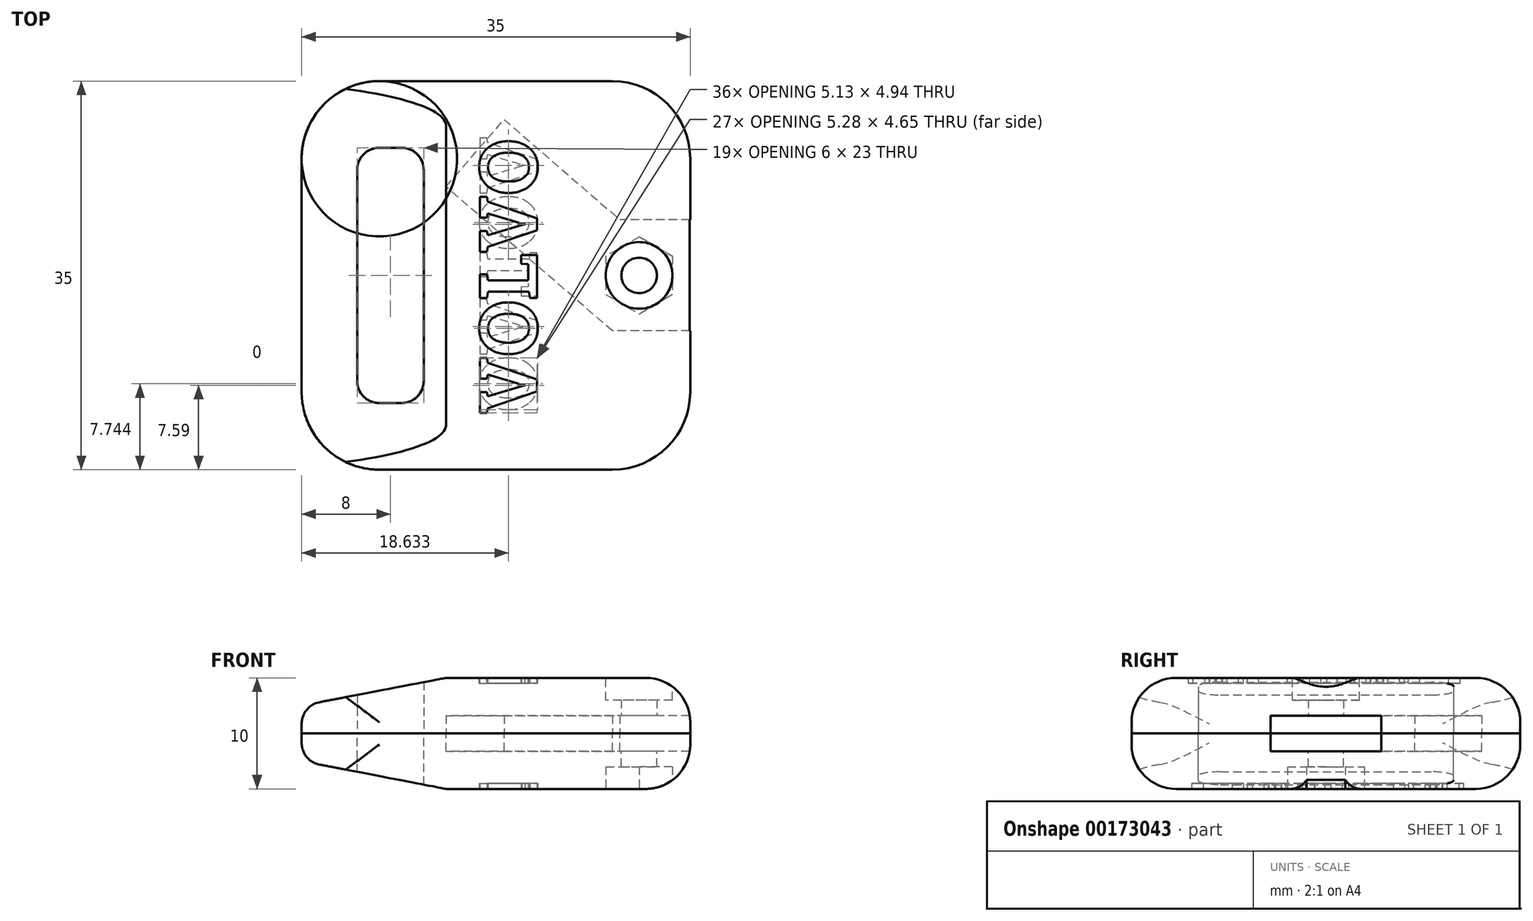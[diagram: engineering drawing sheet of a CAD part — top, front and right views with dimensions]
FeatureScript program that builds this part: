
annotation { "Feature Type Name" : "Feature", "Feature Type Description" : "" }
export const myFeature = defineFeature(function(context is Context, id is Id, definition is map)
    precondition{}
    {
        {
            var Q0;
            Q0=qCreatedBy(makeId("Top.planeOp"),FACE);
            var sketch = newSketch(context, id + "F0", { "sketchPlane" : qUnion([Q0])});
            skLineSegment(sketch, "E0.bottom", {"start": v(7, 0) * mm, "end": v(28, 0) * mm});
            skLineSegment(sketch, "E0.top", {"start": v(7, 35) * mm, "end": v(28, 35) * mm});
            skLineSegment(sketch, "E0.left", {"start": v(0, 7) * mm, "end": v(0, 28) * mm});
            skLineSegment(sketch, "E0.right", {"start": v(35, 7) * mm, "end": v(35, 28) * mm});
            skLineSegment(sketch, "E1.bottom", {"start": v(7, 29) * mm, "end": v(9, 29) * mm});
            skLineSegment(sketch, "E1.top", {"start": v(7, 6) * mm, "end": v(9, 6) * mm});
            skLineSegment(sketch, "E1.left", {"start": v(5, 27) * mm, "end": v(5, 8) * mm});
            skLineSegment(sketch, "E1.right", {"start": v(11, 27) * mm, "end": v(11, 8) * mm});
            skPoint(sketch, "E2.visualSharp", {"position": v(0, 35) * mm});
            skArc(sketch, "E2.filletArc", {"start": v(7, 35) * mm, "mid": v(2.05, 32.95) * mm, "end": v(0, 28) * mm});
            skPoint(sketch, "E3.visualSharp", {"position": v(35, 35) * mm});
            skArc(sketch, "E3.filletArc", {"start": v(35, 28) * mm, "mid": v(32.95, 32.95) * mm, "end": v(28, 35) * mm});
            skPoint(sketch, "E4.visualSharp", {"position": v(35, 0) * mm});
            skArc(sketch, "E4.filletArc", {"start": v(28, 0) * mm, "mid": v(32.95, 2.05) * mm, "end": v(35, 7) * mm});
            skPoint(sketch, "E5.visualSharp", {"position": v(0, 0) * mm});
            skArc(sketch, "E5.filletArc", {"start": v(0, 7) * mm, "mid": v(2.05, 2.05) * mm, "end": v(7, 0) * mm});
            skPoint(sketch, "E6.visualSharp", {"position": v(11, 29) * mm});
            skArc(sketch, "E6.filletArc", {"start": v(11, 27) * mm, "mid": v(10.41, 28.41) * mm, "end": v(9, 29) * mm});
            skPoint(sketch, "E7.visualSharp", {"position": v(11, 6) * mm});
            skArc(sketch, "E7.filletArc", {"start": v(9, 6) * mm, "mid": v(10.41, 6.59) * mm, "end": v(11, 8) * mm});
            skPoint(sketch, "E8.visualSharp", {"position": v(5, 29) * mm});
            skArc(sketch, "E8.filletArc", {"start": v(7, 29) * mm, "mid": v(5.59, 28.41) * mm, "end": v(5, 27) * mm});
            skPoint(sketch, "E9.visualSharp", {"position": v(5, 6) * mm});
            skArc(sketch, "E9.filletArc", {"start": v(5, 8) * mm, "mid": v(5.59, 6.59) * mm, "end": v(7, 6) * mm});
            skLineSegment(sketch, "E10.bottom", {"start": v(35, 12.5) * mm, "end": v(28, 12.5) * mm});
            skLineSegment(sketch, "E10.top", {"start": v(35, 22.5) * mm, "end": v(28, 22.5) * mm});
            skLineSegment(sketch, "E10.left", {"start": v(35, 12.5) * mm, "end": v(35, 22.5) * mm});
            skLineSegment(sketch, "E10.right", {"start": v(28, 12.5) * mm, "end": v(28, 22.5) * mm});
            skLineSegment(sketch, "E11", {"start": v(35, 17.5) * mm, "end": v(0, 17.5) * mm, "construction": true});
            skCircle(sketch, "E12", {"center": v(30.4, 17.5) * mm, "radius": 1.6 * mm});
            skLineSegment(sketch, "E13", {"start": v(28, 12.5) * mm, "end": v(13, 25.5) * mm});
            skLineSegment(sketch, "E14", {"start": v(13, 25.5) * mm, "end": v(18.24, 31.55) * mm});
            skLineSegment(sketch, "E15", {"start": v(18.24, 31.55) * mm, "end": v(28.68, 22.5) * mm});
            skSolve(sketch);
        }
        {
            var Q0;
            Q0=makeQuery(id+"F0.imprint","IMPRINT",FACE,{"disambiguationData":[TD([[makeQuery(id+"F0.imprint","IMPRINT",EDGE,{"derivedFrom":sQuery(id+"F0.wireOp",EDGE,"E0.bottom")}),1.0]])]});
            var Q1;
            {var subQ0=sQuery(id+"F0.wireOp",EDGE,"E10.right");Q1=makeQuery(id+"F0.imprint","IMPRINT",FACE,{"disambiguationData":[TD([[makeQuery(id+"F0.imprint","IMPRINT",EDGE,{"derivedFrom":subQ0}),1.0]])]});}
            var Q2;
            Q2=makeQuery(id+"F0.imprint","IMPRINT",FACE,{"disambiguationData":[TD([[makeQuery(id+"F0.imprint","IMPRINT",EDGE,{"derivedFrom":sQuery(id+"F0.wireOp",EDGE,"E10.bottom")}),-1.0]])]});
            extrude(context, id + "F1", {"entities" : qUnion([Q0, Q1, Q2]), "oppositeDirection" : true, "depth" : 5 * mm});
        }
        {
            var Q0;
            {var subQ0=sQuery(id+"F0.wireOp",EDGE,"E10.right");Q0=makeQuery(id+"F0.imprint","IMPRINT",FACE,{"disambiguationData":[TD([[makeQuery(id+"F0.imprint","IMPRINT",EDGE,{"derivedFrom":subQ0}),1.0]])]});}
            var Q1;
            Q1=makeQuery(id+"F0.imprint","IMPRINT",FACE,{"disambiguationData":[TD([[makeQuery(id+"F0.imprint","IMPRINT",EDGE,{"derivedFrom":sQuery(id+"F0.wireOp",EDGE,"E10.bottom")}),-1.0]])]});
            extrude(context, id + "F2", {"entities" : qUnion([Q0, Q1]), "operationType" : NewBodyOperationType.REMOVE, "oppositeDirection" : true, "depth" : 1.6 * mm});
        }
        {
            var Q0;
            Q0=makeQuery(id+"F0.imprint","IMPRINT",FACE,{"disambiguationData":[TD([[makeQuery(id+"F0.imprint","IMPRINT",EDGE,{"derivedFrom":sQuery(id+"F0.wireOp",EDGE,"E0.bottom")}),1.0]])]});
            var Q1;
            {var subQ0=sQuery(id+"F0.wireOp",EDGE,"E10.right");Q1=makeQuery(id+"F0.imprint","IMPRINT",FACE,{"disambiguationData":[TD([[makeQuery(id+"F0.imprint","IMPRINT",EDGE,{"derivedFrom":subQ0}),1.0]])]});}
            var Q2;
            Q2=makeQuery(id+"F0.imprint","IMPRINT",FACE,{"disambiguationData":[TD([[makeQuery(id+"F0.imprint","IMPRINT",EDGE,{"derivedFrom":sQuery(id+"F0.wireOp",EDGE,"E10.bottom")}),-1.0]])]});
            extrude(context, id + "F3", {"entities" : qUnion([Q0, Q1, Q2]), "depth" : 5 * mm});
        }
        {
            var Q0;
            {var subQ0=sQuery(id+"F0.wireOp",EDGE,"E10.right");Q0=makeQuery(id+"F0.imprint","IMPRINT",FACE,{"disambiguationData":[TD([[makeQuery(id+"F0.imprint","IMPRINT",EDGE,{"derivedFrom":subQ0}),1.0]])]});}
            var Q1;
            Q1=makeQuery(id+"F0.imprint","IMPRINT",FACE,{"disambiguationData":[TD([[makeQuery(id+"F0.imprint","IMPRINT",EDGE,{"derivedFrom":sQuery(id+"F0.wireOp",EDGE,"E10.bottom")}),-1.0]])]});
            extrude(context, id + "F4", {"entities" : qUnion([Q0, Q1]), "operationType" : NewBodyOperationType.REMOVE, "depth" : 1.6 * mm});
        }
        {
            var Q0;
            Q0=makeQuery(id+"F3.opExtrude","CAP_EDGE",EDGE,{"disambiguationData":[OSD([sQuery(id+"F0.wireOp",EDGE,"E0.left")])],"isStart":false});
            chamfer(context, id + "F5", {"entities" : qUnion([Q0]), "chamferType" : ChamferType.TWO_OFFSETS, "width1" : 2.5 * mm, "oppositeDirection" : false, "width2" : 13 * mm});
        }
        {
            var Q0;
            Q0=makeQuery(id+"F1.opExtrude","CAP_EDGE",EDGE,{"disambiguationData":[OSD([sQuery(id+"F0.wireOp",EDGE,"E0.left")])],"isStart":false});
            chamfer(context, id + "F6", {"entities" : qUnion([Q0]), "chamferType" : ChamferType.TWO_OFFSETS, "width1" : 13 * mm, "oppositeDirection" : false, "width2" : 2.5 * mm});
        }
        {
            var Q0;
            Q0=makeQuery(id+"F3.opExtrude","CAP_EDGE",EDGE,{"disambiguationData":[OSD([sQuery(id+"F0.wireOp",EDGE,"E0.bottom")])],"isStart":false});
            var Q1;
            Q1=makeQuery(id+"F1.opExtrude","CAP_EDGE",EDGE,{"disambiguationData":[OSD([sQuery(id+"F0.wireOp",EDGE,"E0.right"),sQuery(id+"F0.wireOp",EDGE,"E10.left")])],"isStart":false});
            fillet(context, id + "F7", {"entities" : qUnion([Q0, Q1]), "radius" : 4 * mm, "tangentPropagation" : true, "allowEdgeOverflow" : false});
        }
        {
            var Q0;
            {var subQ0=sQuery(id+"F0.wireOp",EDGE,"E0.left");Q0=makeQuery(id+"F5.opChamfer","BLEND_EDGE",EDGE,{"blendedFrom":[makeQuery(id+"F3.opExtrude","CAP_EDGE",EDGE,{"disambiguationData":[OSD([subQ0])],"isStart":false}),makeQuery(id+"F3.opExtrude","SWEPT_FACE",FACE,{"disambiguationData":[OSD([subQ0])]})],"blendedInto":[makeQuery(id+"F3.opExtrude","SWEPT_FACE",FACE,{"disambiguationData":[OSD([subQ0])]})]});}
            var Q1;
            {var subQ0=sQuery(id+"F0.wireOp",EDGE,"E0.left");Q1=makeQuery(id+"F6.opChamfer","BLEND_EDGE",EDGE,{"blendedFrom":[makeQuery(id+"F1.opExtrude","CAP_EDGE",EDGE,{"disambiguationData":[OSD([subQ0])],"isStart":false}),makeQuery(id+"F1.opExtrude","SWEPT_FACE",FACE,{"disambiguationData":[OSD([subQ0])]})],"blendedInto":[makeQuery(id+"F1.opExtrude","SWEPT_FACE",FACE,{"disambiguationData":[OSD([subQ0])]})]});}
            fillet(context, id + "F8", {"entities" : qUnion([Q0, Q1]), "radius" : 2 * mm, "allowEdgeOverflow" : false});
        }
        {
            var Q0;
            Q0=makeQuery(id+"F3.opExtrude","CAP_FACE",FACE,{"disambiguationData":[OSD([sQuery(id+"F0.wireOp",EDGE,"E0.bottom"),sQuery(id+"F0.wireOp",EDGE,"E0.top"),sQuery(id+"F0.wireOp",EDGE,"E0.left"),sQuery(id+"F0.wireOp",EDGE,"E0.right"),sQuery(id+"F0.wireOp",EDGE,"E1.bottom"),sQuery(id+"F0.wireOp",EDGE,"E1.top"),sQuery(id+"F0.wireOp",EDGE,"E1.left"),sQuery(id+"F0.wireOp",EDGE,"E1.right"),sQuery(id+"F0.wireOp",EDGE,"E2.filletArc"),sQuery(id+"F0.wireOp",EDGE,"E3.filletArc"),sQuery(id+"F0.wireOp",EDGE,"E4.filletArc"),sQuery(id+"F0.wireOp",EDGE,"E5.filletArc"),sQuery(id+"F0.wireOp",EDGE,"E6.filletArc"),sQuery(id+"F0.wireOp",EDGE,"E7.filletArc"),sQuery(id+"F0.wireOp",EDGE,"E8.filletArc"),sQuery(id+"F0.wireOp",EDGE,"E9.filletArc"),sQuery(id+"F0.wireOp",EDGE,"E10.left"),sQuery(id+"F0.wireOp",EDGE,"E12")])],"isStart":false});
            var sketch = newSketch(context, id + "F9", { "sketchPlane" : qUnion([Q0])});
            skCircle(sketch, "E16", {"center": v(30.4, 17.5) * mm, "radius": 3 * mm});
            skSolve(sketch);
        }
        {
            var Q0;
            {var subQ1=sQuery(id+"F0.wireOp",EDGE,"E12");var subQ10=makeQuery(id+"F3.opExtrude","CAP_EDGE",EDGE,{"disambiguationData":[OSD([subQ1])],"isStart":false});Q0=makeQuery(id+"F9.imprint","IMPRINT",FACE,{"disambiguationData":[TD([[makeQuery(id+"F9.imprint","IMPRINT",EDGE,{"derivedFrom":subQ10}),1.0]])]});}
            var Q1;
            {var subQ1=sQuery(id+"F0.wireOp",EDGE,"E12");var subQ10=makeQuery(id+"F3.opExtrude","CAP_EDGE",EDGE,{"disambiguationData":[OSD([subQ1])],"isStart":false});Q1=makeQuery(id+"F9.imprint","IMPRINT",FACE,{"disambiguationData":[TD([[makeQuery(id+"F9.imprint","IMPRINT",EDGE,{"derivedFrom":subQ10}),-1.0]])]});}
            extrude(context, id + "F10", {"entities" : qUnion([Q0, Q1]), "operationType" : NewBodyOperationType.REMOVE, "oppositeDirection" : true, "depth" : 2 * mm});
        }
        {
            var Q0;
            Q0=makeQuery(id+"F1.opExtrude","CAP_FACE",FACE,{"disambiguationData":[OSD([sQuery(id+"F0.wireOp",EDGE,"E0.bottom"),sQuery(id+"F0.wireOp",EDGE,"E0.top"),sQuery(id+"F0.wireOp",EDGE,"E0.left"),sQuery(id+"F0.wireOp",EDGE,"E0.right"),sQuery(id+"F0.wireOp",EDGE,"E1.bottom"),sQuery(id+"F0.wireOp",EDGE,"E1.top"),sQuery(id+"F0.wireOp",EDGE,"E1.left"),sQuery(id+"F0.wireOp",EDGE,"E1.right"),sQuery(id+"F0.wireOp",EDGE,"E2.filletArc"),sQuery(id+"F0.wireOp",EDGE,"E3.filletArc"),sQuery(id+"F0.wireOp",EDGE,"E4.filletArc"),sQuery(id+"F0.wireOp",EDGE,"E5.filletArc"),sQuery(id+"F0.wireOp",EDGE,"E6.filletArc"),sQuery(id+"F0.wireOp",EDGE,"E7.filletArc"),sQuery(id+"F0.wireOp",EDGE,"E8.filletArc"),sQuery(id+"F0.wireOp",EDGE,"E9.filletArc"),sQuery(id+"F0.wireOp",EDGE,"E10.left"),sQuery(id+"F0.wireOp",EDGE,"E12")])],"isStart":false});
            var sketch = newSketch(context, id + "F11", { "sketchPlane" : qUnion([Q0])});
            skCircle(sketch, "E17.cCircle", {"center": v(30.4, -17.5) * mm, "radius": 3 * mm, "construction": true});
            skLineSegment(sketch, "E17.0", {"start": v(33.4, -19.23) * mm, "end": v(30.4, -20.96) * mm});
            skLineSegment(sketch, "E17.1", {"start": v(30.4, -20.96) * mm, "end": v(27.4, -19.23) * mm});
            skLineSegment(sketch, "E17.2", {"start": v(27.4, -19.23) * mm, "end": v(27.4, -15.77) * mm});
            skLineSegment(sketch, "E17.3", {"start": v(27.4, -15.77) * mm, "end": v(30.4, -14.04) * mm});
            skLineSegment(sketch, "E17.4", {"start": v(30.4, -14.04) * mm, "end": v(33.4, -15.77) * mm});
            skLineSegment(sketch, "E17.5", {"start": v(33.4, -15.77) * mm, "end": v(33.4, -19.23) * mm});
            skPoint(sketch, "E17.0.midPoint", {"position": v(31.9, -20.1) * mm});
            skSolve(sketch);
        }
        {
            var Q0;
            {var subQ3=sQuery(id+"F11.wireOp",EDGE,"E17.1");Q0=makeQuery(id+"F11.imprint","IMPRINT",FACE,{"disambiguationData":[TD([[makeQuery(id+"F11.imprint","IMPRINT",EDGE,{"derivedFrom":subQ3}),-1.0]])]});}
            var Q1;
            {var subQ0=sQuery(id+"F11.wireOp",EDGE,"E17.5");Q1=makeQuery(id+"F11.imprint","IMPRINT",FACE,{"disambiguationData":[TD([[makeQuery(id+"F11.imprint","IMPRINT",EDGE,{"derivedFrom":subQ0}),-1.0]])]});}
            extrude(context, id + "F12", {"entities" : qUnion([Q0, Q1]), "operationType" : NewBodyOperationType.REMOVE, "oppositeDirection" : true, "depth" : 2 * mm});
        }
        {
            var Q0;
            Q0=makeQuery(id+"F3.opExtrude","CAP_FACE",FACE,{"disambiguationData":[OSD([sQuery(id+"F0.wireOp",EDGE,"E0.bottom"),sQuery(id+"F0.wireOp",EDGE,"E0.top"),sQuery(id+"F0.wireOp",EDGE,"E0.left"),sQuery(id+"F0.wireOp",EDGE,"E0.right"),sQuery(id+"F0.wireOp",EDGE,"E1.bottom"),sQuery(id+"F0.wireOp",EDGE,"E1.top"),sQuery(id+"F0.wireOp",EDGE,"E1.left"),sQuery(id+"F0.wireOp",EDGE,"E1.right"),sQuery(id+"F0.wireOp",EDGE,"E2.filletArc"),sQuery(id+"F0.wireOp",EDGE,"E3.filletArc"),sQuery(id+"F0.wireOp",EDGE,"E4.filletArc"),sQuery(id+"F0.wireOp",EDGE,"E5.filletArc"),sQuery(id+"F0.wireOp",EDGE,"E6.filletArc"),sQuery(id+"F0.wireOp",EDGE,"E7.filletArc"),sQuery(id+"F0.wireOp",EDGE,"E8.filletArc"),sQuery(id+"F0.wireOp",EDGE,"E9.filletArc"),sQuery(id+"F0.wireOp",EDGE,"E10.left"),sQuery(id+"F0.wireOp",EDGE,"E12")])],"isStart":false});
            var sketch = newSketch(context, id + "F13", { "sketchPlane" : qUnion([Q0])});
            skText(sketch, "E18", { "text": "VOLVO", "fontName": "RobotoSlab-Bold.ttf"});
            const initialGuessF13  = {"E18": [0.0212, 0.005, 0, 1, 0.0052]};
            skSetInitialGuess(sketch, initialGuessF13);
            skSolve(sketch);
        }
        {
            var Q0;
            Q0 = qSketchRegion(id + "F13", true);
            extrude(context, id + "F14", {"entities" : qUnion([Q0]), "operationType" : NewBodyOperationType.REMOVE, "oppositeDirection" : true, "depth" : 0.5 * mm});
        }
        {
            var Q0;
            Q0=makeQuery(id+"F1.opExtrude","CAP_FACE",FACE,{"disambiguationData":[OSD([sQuery(id+"F0.wireOp",EDGE,"E0.bottom"),sQuery(id+"F0.wireOp",EDGE,"E0.top"),sQuery(id+"F0.wireOp",EDGE,"E0.left"),sQuery(id+"F0.wireOp",EDGE,"E0.right"),sQuery(id+"F0.wireOp",EDGE,"E1.bottom"),sQuery(id+"F0.wireOp",EDGE,"E1.top"),sQuery(id+"F0.wireOp",EDGE,"E1.left"),sQuery(id+"F0.wireOp",EDGE,"E1.right"),sQuery(id+"F0.wireOp",EDGE,"E2.filletArc"),sQuery(id+"F0.wireOp",EDGE,"E3.filletArc"),sQuery(id+"F0.wireOp",EDGE,"E4.filletArc"),sQuery(id+"F0.wireOp",EDGE,"E5.filletArc"),sQuery(id+"F0.wireOp",EDGE,"E6.filletArc"),sQuery(id+"F0.wireOp",EDGE,"E7.filletArc"),sQuery(id+"F0.wireOp",EDGE,"E8.filletArc"),sQuery(id+"F0.wireOp",EDGE,"E9.filletArc"),sQuery(id+"F0.wireOp",EDGE,"E10.left"),sQuery(id+"F0.wireOp",EDGE,"E12")])],"isStart":false});
            var sketch = newSketch(context, id + "F15", { "sketchPlane" : qUnion([Q0])});
            skText(sketch, "E19", { "text": "VOLVO", "fontName": "RobotoSlab-Bold.ttf"});
            const initialGuessF15  = {"E19": [0.0212, -0.03, 0, 1, 0.0052]};
            skSetInitialGuess(sketch, initialGuessF15);
            skSolve(sketch);
        }
        {
            var Q0;
            Q0 = qSketchRegion(id + "F15", true);
            extrude(context, id + "F16", {"entities" : qUnion([Q0]), "operationType" : NewBodyOperationType.REMOVE, "oppositeDirection" : true, "depth" : 0.5 * mm});
        }
    });
